# Revit family: Ventüer_VentilationLouvres_VL-3SD
name_source: partatom
category: Generic Models
units: mm (PartAtom-declared; Revit-internal decimal feet)

## family parameters
Always vertical = No
Can host rebar = No
Cut with Voids When Loaded = No
Part Type = Normal
Room Calculation Point = No
Round Connector Dimension = Use Diameter
Shared = No
Work Plane-Based = Yes

## types (3) — shared parameters
Aerodynamic Performance = Air Inlet: 0.247, Class 3. Air Extract: 0.260, Class 3
Ancillaries = Bird Mesh, Insect Mesh, Solid Blanking, Perimeter Mounting Angle
Blade And Frame Gap = 16 mm  [stored 0.0524934 ft]
Blade Centres = 50 mm  [stored 0.164042 ft]
Blade Count = 10
Blade Cut Offset = 500 mm  [stored 1.64042 ft]
Blade Material = Ventüer Aluminium
Default Elevation = 1219 mm
Description = Ultimate Weather Protection Louvre
Exact Neck Height = 594 mm  [stored 1.94882 ft]
Exact Neck Height Check = 594 mm  [stored 1.94882 ft]
Exact Neck Width = 594 mm  [stored 1.94882 ft]
Exact Neck Width Check = 594 mm  [stored 1.94882 ft]
Frame Material = Ventüer Aluminium
Frame Set Count = 1
Frame Set Count Check = 2
Frame Set Transition Count = 1
Frame Set Transition Count Check = 2
Manufacturer = Ventüer
Max Flow = 5000.0 L/s
Min Flow = 100.0 L/s
Model = VL-3SD
Multiple Frame Set = No
Multiple Transition = No
Noise Level NC Max = 0.00 NC
Noise Level NC Min = 0.00 NC
Nominal Height = 600 mm
Nominal Width = 600 mm
Nominated Air Flow = 100.0 L/s
Nominated Pessure Drop = 21.0 Pa
Rain Defence Performance = Class A - up to 1.5m/s suction velocity. Class B - up to 3.5m/s suction velocity
Rear Frame Set Offset = 16 mm  [stored 0.0524934 ft]
Single Frame Set = Yes
Single Transition = No
Specified Air Flow = 0.0 L/s
Specified Pressure Drop = 21.0 Pa
Static Pressure Max = 60.0 Pa
Static Pressure Min = 10.0 Pa
URL = https://www.ventuer.co
Ventüer Product Range = Ventilation Louvres

## per-type parameters (varying)
| type | Base Width | Channel | Connector Height | Connector Width | Depth | Flanged | Frame Set Height | Frame Set Width | Glazed | Overall Opening Height | Overall Opening Width | Profile Width | Rear Mullion Offset | Single Frame Set Width | Top Blade Height |
| VL-3SD_FF | 25 mm  [stored 0.082021 ft] | No | 544 mm | 544 mm | 160 mm  [stored 0.524934 ft] | Yes | 544 mm | 544 mm | No | 544 mm | 544 mm | 25 mm  [stored 0.082021 ft] | 2 mm  [stored 0.00656168 ft] | 272 mm | 28 mm |
| VL-3SD_GF | 26 mm | No | 542 mm  [stored 1.77822 ft] | 542 mm  [stored 1.77822 ft] | 155 mm  [stored 0.50853 ft] | No | 542 mm  [stored 1.77822 ft] | 542 mm  [stored 1.77822 ft] | Yes | 542 mm  [stored 1.77822 ft] | 542 mm  [stored 1.77822 ft] | 26 mm | 6 mm  [stored 0.019685 ft] | 271 mm  [stored 0.889108 ft] | 26 mm |
| VL-3SD_CF | 25 mm  [stored 0.082021 ft] | Yes | 567 mm | 589 mm | 150 mm | No | 567 mm | 589 mm | No | 567 mm | 589 mm | 3 mm  [stored 0.00984252 ft] | 2 mm  [stored 0.00656168 ft] | 295 mm | 50 mm  [stored 0.164042 ft] |

note: column(s) folded — value = type name in every type: Keynote

note: [stored X ft] marks values corroborated as IEEE doubles in the binary element streams (Revit-internal decimal feet)

## geometry (parser evidence)
native form markers: Sweep x38
no freeform markers — native parametric forms only
